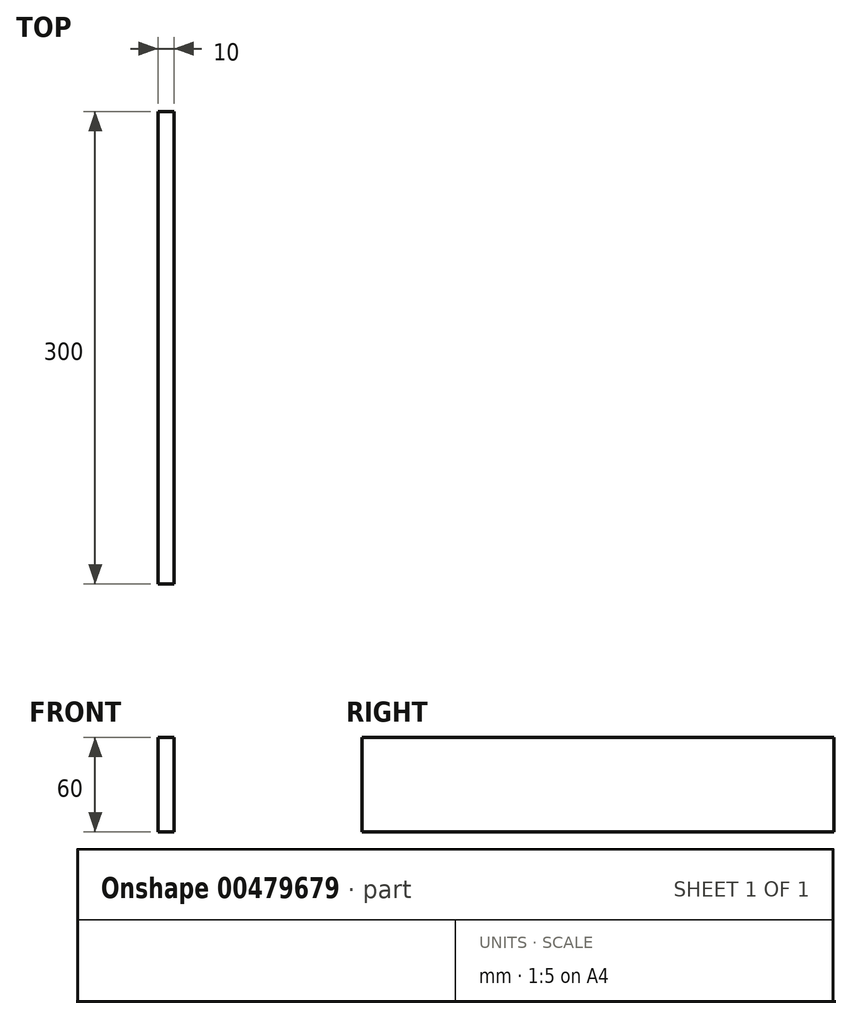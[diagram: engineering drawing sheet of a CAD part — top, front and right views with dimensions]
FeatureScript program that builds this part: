
annotation { "Feature Type Name" : "Feature", "Feature Type Description" : "" }
export const myFeature = defineFeature(function(context is Context, id is Id, definition is map)
    precondition{}
    {
        {
            var Q0;
            Q0=qCreatedBy(makeId("Front.planeOp"),FACE);
            var sketch = newSketch(context, id + "F0", { "sketchPlane" : qUnion([Q0])});
            skLineSegment(sketch, "E0.bottom", {"start": v(5, 30) * mm, "end": v(-5, 30) * mm});
            skLineSegment(sketch, "E0.top", {"start": v(5, -30) * mm, "end": v(-5, -30) * mm});
            skLineSegment(sketch, "E0.left", {"start": v(5, 30) * mm, "end": v(5, -30) * mm});
            skLineSegment(sketch, "E0.right", {"start": v(-5, 30) * mm, "end": v(-5, -30) * mm});
            skPoint(sketch, "E0.middle", {"position": v(0, 0) * mm});
            skSolve(sketch);
        }
        {
            var Q0;
            Q0 = qSketchRegion(id + "F0", true);
            extrude(context, id + "F1", {"entities" : qUnion([Q0]), "endBound" : BoundingType.SYMMETRIC, "depth" : 300 * mm});
        }
    });
